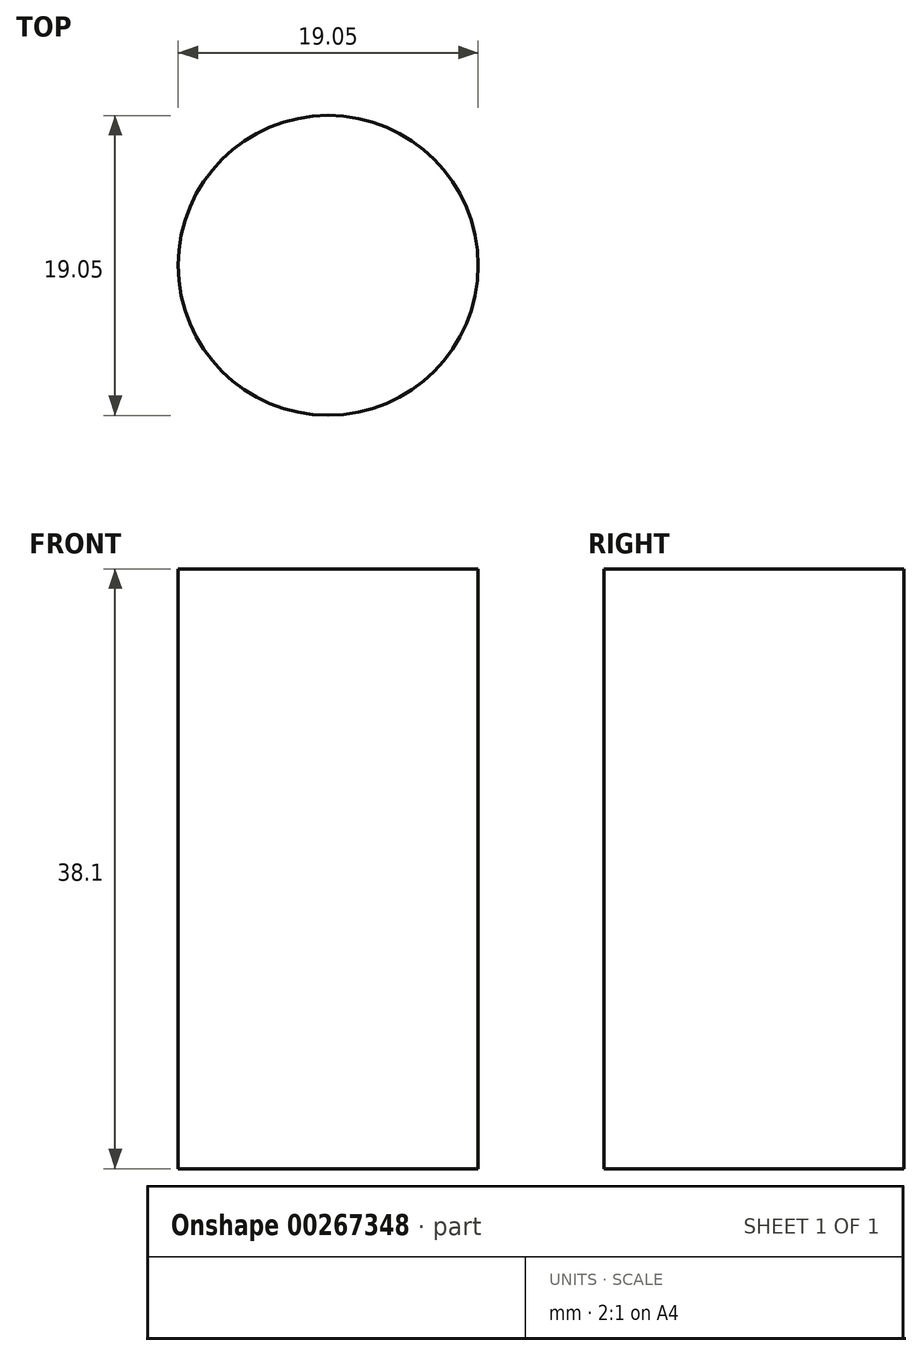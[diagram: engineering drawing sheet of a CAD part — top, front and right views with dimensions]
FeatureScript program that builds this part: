
annotation { "Feature Type Name" : "Feature", "Feature Type Description" : "" }
export const myFeature = defineFeature(function(context is Context, id is Id, definition is map)
    precondition{}
    {
        {
            var Q0;
            Q0=qCreatedBy(makeId("Top.planeOp"),FACE);
            var sketch = newSketch(context, id + "F0", { "sketchPlane" : qUnion([Q0])});
            skCircle(sketch, "E0", {"center": v(-103.1, -23.45) * mm, "radius": 9.53 * mm});
            skPoint(sketch, "E1", {"position": v(-103.1, -32.98) * mm});
            skPoint(sketch, "E2", {"position": v(-103.1, -13.93) * mm});
            skSolve(sketch);
        }
        {
            var Q0;
            Q0=makeQuery(id+"F0.imprint","IMPRINT",FACE,{"disambiguationData":[TD([[makeQuery(id+"F0.imprint","IMPRINT",EDGE,{"derivedFrom":sQuery(id+"F0.wireOp",EDGE,"E0")}),1.0]])]});
            extrude(context, id + "F1", {"entities" : qUnion([Q0]), "depth" : 38.1 * mm});
        }
    });
